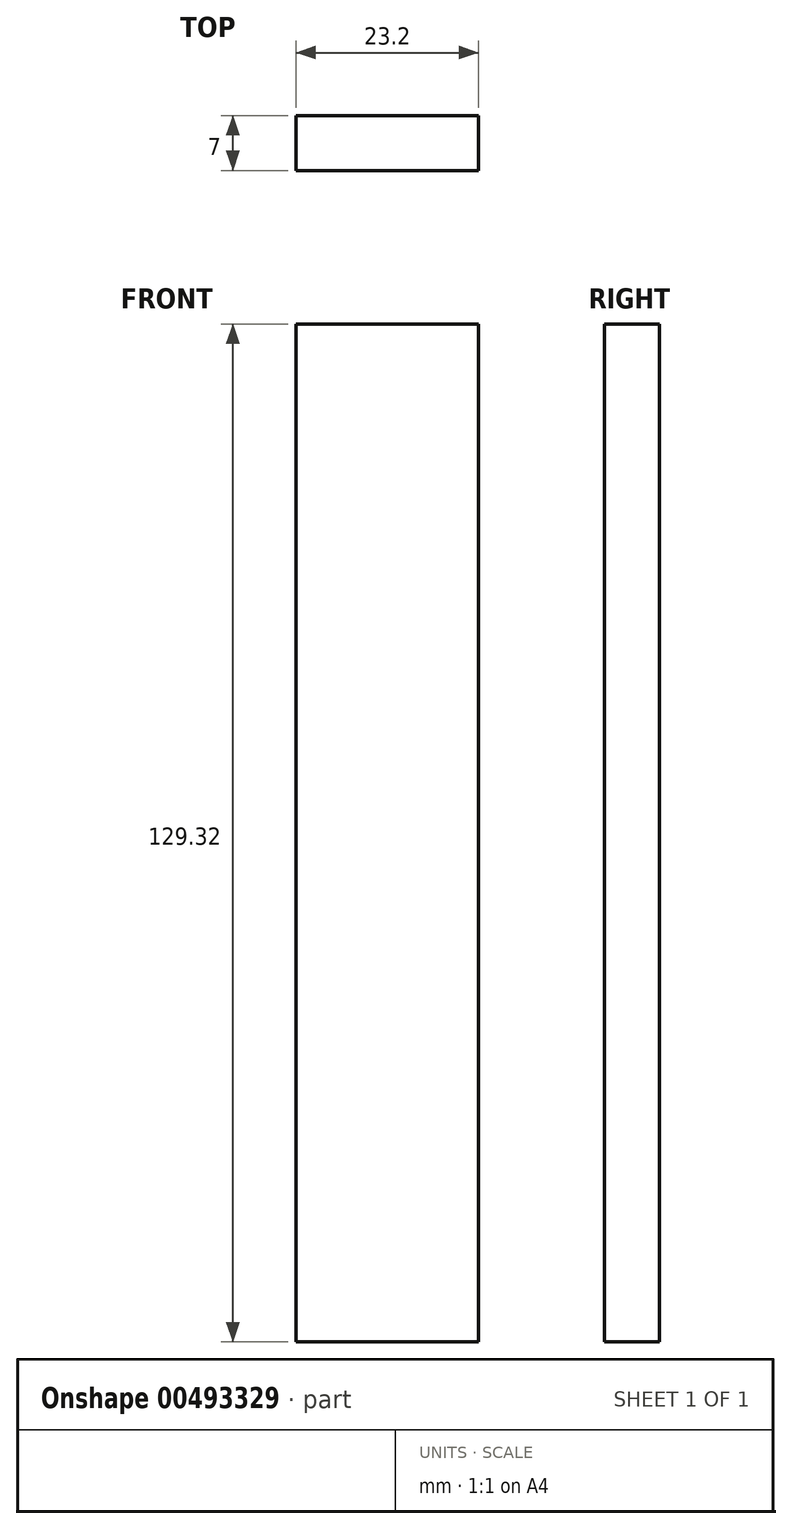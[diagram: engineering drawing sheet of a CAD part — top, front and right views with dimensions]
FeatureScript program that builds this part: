
annotation { "Feature Type Name" : "Feature", "Feature Type Description" : "" }
export const myFeature = defineFeature(function(context is Context, id is Id, definition is map)
    precondition{}
    {
        {
            var Q0;
            Q0=qCreatedBy(makeId("Front.planeOp"),FACE);
            var sketch = newSketch(context, id + "F0", { "sketchPlane" : qUnion([Q0])});
            skLineSegment(sketch, "E0.bottom", {"start": v(11.6, 64.66) * mm, "end": v(-11.6, 64.66) * mm});
            skLineSegment(sketch, "E0.top", {"start": v(11.6, -64.66) * mm, "end": v(-11.6, -64.66) * mm});
            skLineSegment(sketch, "E0.left", {"start": v(11.6, 64.66) * mm, "end": v(11.6, -64.66) * mm});
            skLineSegment(sketch, "E0.right", {"start": v(-11.6, 64.66) * mm, "end": v(-11.6, -64.66) * mm});
            skPoint(sketch, "E0.middle", {"position": v(0, 0) * mm});
            skSolve(sketch);
        }
        {
            var Q0;
            Q0=makeQuery(id+"F0.imprint","IMPRINT",FACE,{"disambiguationData":[TD([[makeQuery(id+"F0.imprint","IMPRINT",EDGE,{"derivedFrom":sQuery(id+"F0.wireOp",EDGE,"E0.bottom")}),1.0]])]});
            extrude(context, id + "F1", {"entities" : qUnion([Q0]), "endBound" : BoundingType.SYMMETRIC, "depth" : 7 * mm});
        }
    });
